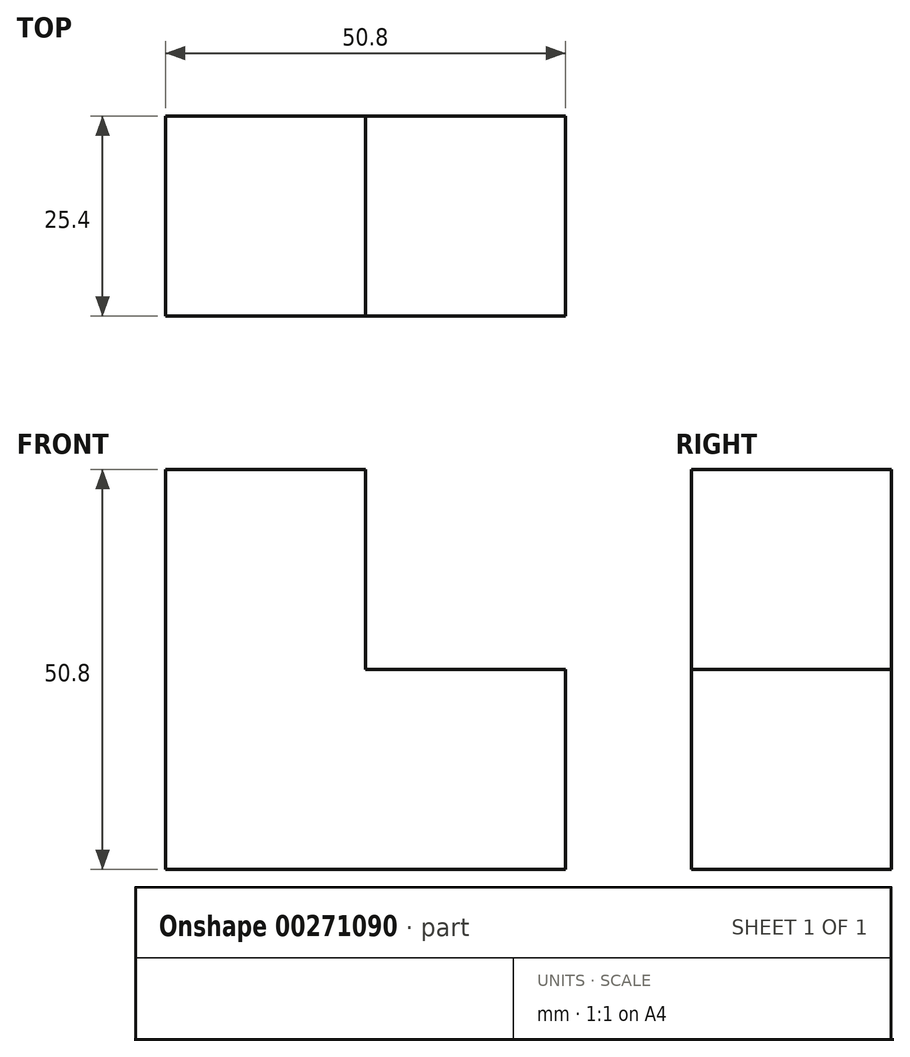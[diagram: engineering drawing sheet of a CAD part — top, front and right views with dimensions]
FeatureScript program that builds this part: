
annotation { "Feature Type Name" : "Feature", "Feature Type Description" : "" }
export const myFeature = defineFeature(function(context is Context, id is Id, definition is map)
    precondition{}
    {
        {
            var Q0;
            Q0=qCreatedBy(makeId("Front.planeOp"),FACE);
            var sketch = newSketch(context, id + "F0", { "sketchPlane" : qUnion([Q0])});
            skLineSegment(sketch, "E0", {"start": v(0, 0) * mm, "end": v(0, 50.8) * mm});
            skLineSegment(sketch, "E1", {"start": v(0, 50.8) * mm, "end": v(25.4, 50.8) * mm});
            skLineSegment(sketch, "E2", {"start": v(25.4, 50.8) * mm, "end": v(25.4, 25.4) * mm});
            skLineSegment(sketch, "E3", {"start": v(25.4, 25.4) * mm, "end": v(50.8, 25.4) * mm});
            skLineSegment(sketch, "E4", {"start": v(50.8, 25.4) * mm, "end": v(50.8, 0) * mm});
            skLineSegment(sketch, "E5", {"start": v(50.8, 0) * mm, "end": v(0, 0) * mm});
            skSolve(sketch);
        }
        {
            var Q0;
            Q0=makeQuery(id+"F0.imprint","IMPRINT",FACE,{"disambiguationData":[TD([[makeQuery(id+"F0.imprint","IMPRINT",EDGE,{"derivedFrom":sQuery(id+"F0.wireOp",EDGE,"E0")}),-1.0]])]});
            extrude(context, id + "F1", {"entities" : qUnion([Q0]), "depth" : 25.4 * mm});
        }
    });
